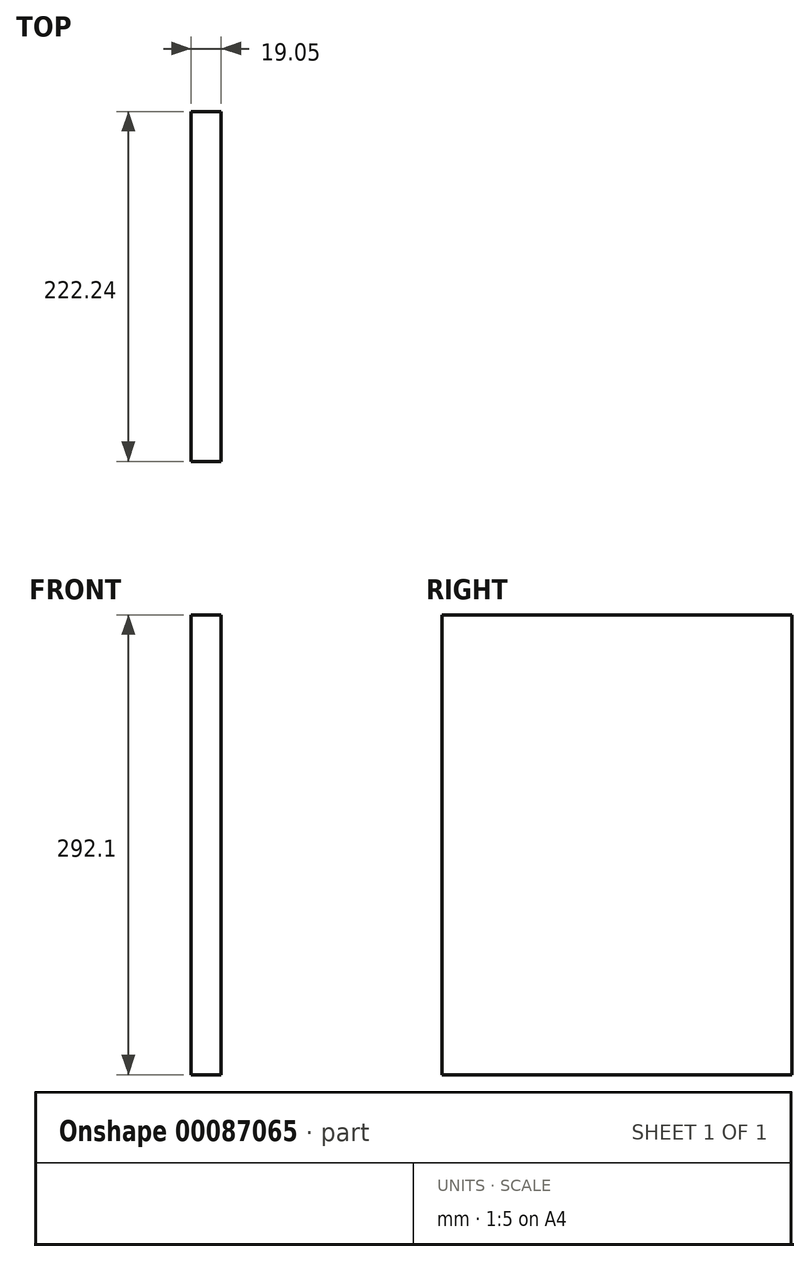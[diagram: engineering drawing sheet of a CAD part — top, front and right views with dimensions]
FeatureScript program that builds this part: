
annotation { "Feature Type Name" : "Feature", "Feature Type Description" : "" }
export const myFeature = defineFeature(function(context is Context, id is Id, definition is map)
    precondition{}
    {
        {
            var Q0;
            Q0=qCreatedBy(makeId("Right.planeOp"),FACE);
            var sketch = newSketch(context, id + "F0", { "sketchPlane" : qUnion([Q0])});
            skLineSegment(sketch, "E0.bottom", {"start": v(-111.12, 146.05) * mm, "end": v(111.13, 146.05) * mm});
            skLineSegment(sketch, "E0.top", {"start": v(-111.13, -146.05) * mm, "end": v(111.12, -146.05) * mm});
            skLineSegment(sketch, "E0.left", {"start": v(-111.12, 146.05) * mm, "end": v(-111.13, -146.05) * mm});
            skLineSegment(sketch, "E0.right", {"start": v(111.13, 146.05) * mm, "end": v(111.12, -146.05) * mm});
            skPoint(sketch, "E0.middle", {"position": v(0, 0) * mm});
            skSolve(sketch);
        }
        {
            var Q0;
            Q0=makeQuery(id+"F0.imprint","IMPRINT",FACE,{"disambiguationData":[TD([[makeQuery(id+"F0.imprint","IMPRINT",EDGE,{"derivedFrom":sQuery(id+"F0.wireOp",EDGE,"E0.bottom")}),-1.0]])]});
            extrude(context, id + "F1", {"entities" : qUnion([Q0]), "depth" : 19.05 * mm});
        }
    });
